# Revit family: 58149113(2021)
name_source: partatom
category: Plumbing Fixtures
units: mm (PartAtom-declared; Revit-internal decimal feet)

## family parameters
Always vertical = Yes
Cut with Voids When Loaded = No
OmniClass Number = 23.45.55.00
OmniClass Title = Sanitary Faucets, Wastes
Part Type = Normal
Room Calculation Point = No
Round Connector Dimension = Use Diameter
Shared = No
Work Plane-Based = No

## types (1)
- 58149113 Shower system
    2D/3D/BIM Files URL = http://static.hansa.com
    3D View = https://static.hansa.com
    Advanced Features = Inner body made of DZR brass;Flexible length / can be shortened
    AssetType = Fixed
    BIMObjectName = 58149113(2021)
    Backflow Prevention EN1717 = EB
    BodyMaterial = Brass
    Brand = HANSA
    CO2 Emissions (A1-A3) = 27.68
    CO2 Emissions (A4) = 0.73
    CO2 Emissions (B7) = 2316
    CO2 Emissions (C2) = 0.05
    CO2 Emissions (C3) = 0.05
    CO2 Emissions (C4) = 1.52
    CO2 Emissions (D) = -18.09
    Catalog Drawing URL = http://static.hansa.com
    Category = Shower solutions
    CloseOffRating = 0
    Color = Chrome
    Connection = Eccentric coupling(s);Cover plate(s);Silencer(s)
    Connection Size = G1/2
    Default Elevation = 0 mm  [stored 0 ft]
    Dimension Drawing URL = http://static.hansa.com
    Diverter = Integrated into flow control handle
    DurationUnit = Year
    EAN Number = 4057304016080
    EN Standard = EN 1111, EN 1112, EN 1113
    ETIM Class Number = EC011329 Shower mixing tap
    FDV Document URL = http://www.hansa.com
    FaucetMainMaterial = Brass
    Features = Thermostatic
    Finish = Polished
    Flow Drawing URL = http://static.hansa.com
    Flow Rate At 300kPa = 0.2 L/s
    FlowCoefficient = 0
    Group = Shower system
    Hand Shower Size = Ø 95 mm
    IfcExportAs = IfcValveType
    IfcExportType = FAUCET
    Installation Type = Wall mounted
    Installation Width = CC150± 15 mm
    Installation and Maintenance Guide URL = http://static.hansa.com
    Interactive AR View URL = https://static.hansa.com
    Lever Handle = Temperature control handle;Flow control handle
    Manufacturer = HANSA
    ManufacturerName = HANSA
    ManufacturerURL = http://www.hansa.com
    Market = International;Germany;Austria;Belgium;Netherlands;France;Czech Republic;Slovakia;Italy;Spain
    Material = Brass
    Max. Hot Water Supply = 80 °C
    Mechanical Parts = Ceramic head part for flow control;Thermostatic cartridge for automatic temperature control;Non-return valve(s);Litter filter(s)
    Mobile Product Information URL = http://mpi.hansa.com
    Model = 58149113 Shower system
    ModelReference = 58149113
    NBSDescription = Shower mixers
    NBSReference = 45-35-70/335
    Name = 58149113 Shower system
    Name_en = 58149113 Shower system
    Noise Class = I (ISO 3822)
    NominalDepth = 595 mm
    NominalHeight = 1144 mm
    NominalWidth = 300 mm
    Over Head Shower Size = 200 x 200 mm
    Pressure Loss With Flow 02ls = 265000.0 Pa
    Product Code = 58149113
    Product Family = HANSAUNITA
    Product Image URL = http://static.hansa.com
    Product URL = http://static.hansa.com
    Sales Package dimensions (LxWxH) = 838 x 308 x 81
    Shape = Sculptured
    Shower Parts = Hand shower;Shower rail;Overhead shower;Adjustable shower rail bracket;Shower hose (1250 mm);Eco flow control
    Shower Spray = Normal;Refreshing;Relaxing
    Shower Spray Number = 3 shower sprays
    ShowerDefaultElevation = 900 mm
    Size = 300x595x1145 mm
    Spare-Part Information URL = http://static.hansa.com
    Spout Projection = 470 - 495 mm
    Surface treatment = Chrome
    Technical DataSheet URL = http://www.hansa.com
    Temperature Adjustments = Safety stop against scalding at 38°C;The housing of the fittings conducts minimal heat
    UNSPSC Class Number = 30181503 Showers
    URL Declaration Of Performance (DOP) = http://static.hansa.com
    URL Declaration of Asbestos = http://static.hansa.com
    URL Declaration of Conformity = http://static.hansa.com
    URL Declaration of SCIP = http://static.hansa.com
    URL EU Packaging Declaration = http://static.hansa.com
    URL EcoLabel Declaration = http://static.hansa.com
    URL Environmental Product Declaration EPD = http://www.hansa.com system.pdf
    URL Materials Declaration = http://www.hansa.com
    URL REACH = http://static.hansa.com
    URL UWL = http://static.hansa.com
    Uniclass2 = Pr_40_30_96_81
    Uniclass2015Description = Shower thermostatic water supply sets
    Uniclass2015Reference = Pr_40_20_87_81
    Version = 1
    VersionDate = 01/06/2023
    Warranty Information URL = http://warranty.hansa.com
    WarrantyDescription = http://warranty.hansa.com
    WarrantyDurationUnit = Year
    Working Pressure = 50 - 1000 kPa

note: [stored X ft] marks values corroborated as IEEE doubles in the binary element streams (Revit-internal decimal feet)

## geometry (parser evidence)
native form markers: Sweep x6
no freeform markers — native parametric forms only
